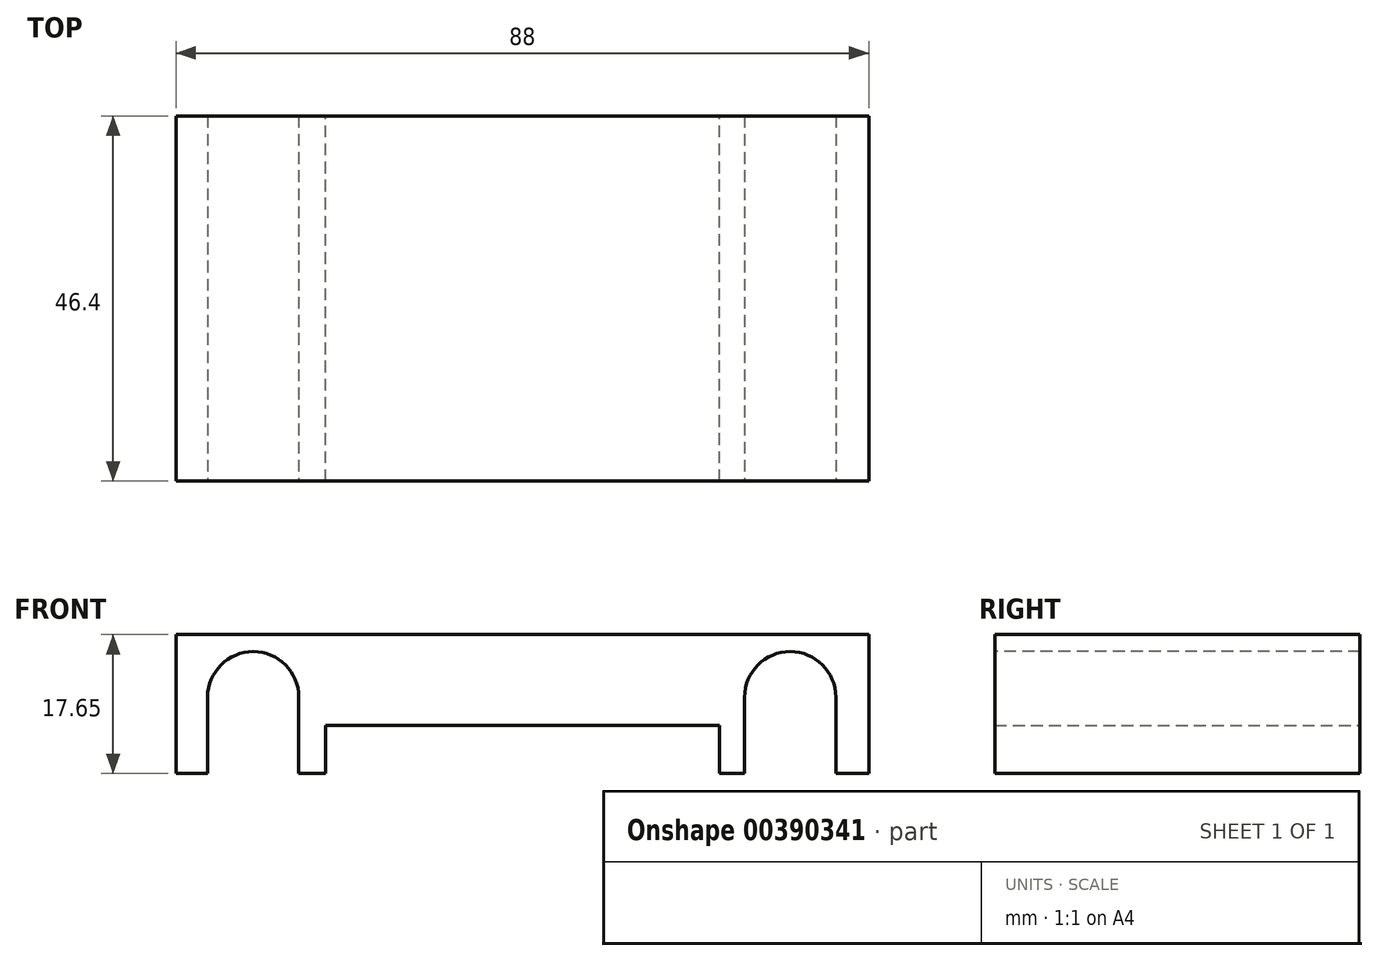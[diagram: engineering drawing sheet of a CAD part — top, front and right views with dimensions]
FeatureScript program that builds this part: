
annotation { "Feature Type Name" : "Feature", "Feature Type Description" : "" }
export const myFeature = defineFeature(function(context is Context, id is Id, definition is map)
    precondition{}
    {
        {
            var Q0;
            Q0=qCreatedBy(makeId("Top.planeOp"),FACE);
            var sketch = newSketch(context, id + "F0", { "sketchPlane" : qUnion([Q0])});
            skLineSegment(sketch, "E0.bottom", {"start": v(44, 23.2) * mm, "end": v(-44, 23.2) * mm});
            skLineSegment(sketch, "E0.top", {"start": v(44, -23.2) * mm, "end": v(-44, -23.2) * mm});
            skLineSegment(sketch, "E0.left", {"start": v(44, 23.2) * mm, "end": v(44, -23.2) * mm});
            skLineSegment(sketch, "E0.right", {"start": v(-44, 23.2) * mm, "end": v(-44, -23.2) * mm});
            skPoint(sketch, "E0.middle", {"position": v(0, 0) * mm});
            skSolve(sketch);
        }
        {
            var Q0;
            Q0 = qSketchRegion(id + "F0", true);
            extrude(context, id + "F1", {"entities" : qUnion([Q0]), "oppositeDirection" : true, "depth" : 17.65 * mm});
        }
        {
            var Q0;
            Q0=makeQuery(id+"F1.opExtrude","CAP_FACE",FACE,{"disambiguationData":[OSD([sQuery(id+"F0.wireOp",EDGE,"E0.bottom"),sQuery(id+"F0.wireOp",EDGE,"E0.top"),sQuery(id+"F0.wireOp",EDGE,"E0.left"),sQuery(id+"F0.wireOp",EDGE,"E0.right")])],"isStart":false});
            var sketch = newSketch(context, id + "F2", { "sketchPlane" : qUnion([Q0])});
            skLineSegment(sketch, "E1.bottom", {"start": v(-25, 23.2) * mm, "end": v(25, 23.2) * mm});
            skLineSegment(sketch, "E1.top", {"start": v(-25, -23.2) * mm, "end": v(25, -23.2) * mm});
            skLineSegment(sketch, "E1.left", {"start": v(-25, 23.2) * mm, "end": v(-25, -23.2) * mm});
            skLineSegment(sketch, "E1.right", {"start": v(25, 23.2) * mm, "end": v(25, -23.2) * mm});
            skSolve(sketch);
        }
        {
            var Q0;
            Q0 = qSketchRegion(id + "F2", true);
            extrude(context, id + "F3", {"entities" : qUnion([Q0]), "operationType" : NewBodyOperationType.REMOVE, "oppositeDirection" : true, "depth" : 6.15 * mm});
        }
        {
            var Q0;
            Q0=qCreatedBy(makeId("Front.planeOp"),FACE);
            var sketch = newSketch(context, id + "F4", { "sketchPlane" : qUnion([Q0])});
            skLineSegment(sketch, "E2.0.0", {"start": v(-25, -11.5) * mm, "end": v(25, -11.5) * mm, "construction": true});
            skLineSegment(sketch, "E2.0.1", {"start": v(25, -11.5) * mm, "end": v(25, -17.65) * mm, "construction": true});
            skLineSegment(sketch, "E2.0.2", {"start": v(25, -17.65) * mm, "end": v(44, -17.65) * mm, "construction": true});
            skLineSegment(sketch, "E2.0.3", {"start": v(44, -17.65) * mm, "end": v(44, 0) * mm, "construction": true});
            skLineSegment(sketch, "E2.0.4", {"start": v(44, 0) * mm, "end": v(-44, 0) * mm, "construction": true});
            skLineSegment(sketch, "E2.0.5", {"start": v(-44, 0) * mm, "end": v(-44, -17.65) * mm, "construction": true});
            skLineSegment(sketch, "E2.0.6", {"start": v(-44, -17.65) * mm, "end": v(-25, -17.65) * mm, "construction": true});
            skLineSegment(sketch, "E2.0.7", {"start": v(-25, -17.65) * mm, "end": v(-25, -11.5) * mm, "construction": true});
            skLineSegment(sketch, "E3.bottom", {"start": v(-40, -17.65) * mm, "end": v(-28.4, -17.65) * mm});
            skLineSegment(sketch, "E3.top", {"start": v(-40, -7.95) * mm, "end": v(-28.4, -7.95) * mm, "construction": true});
            skLineSegment(sketch, "E3.left", {"start": v(-40, -17.65) * mm, "end": v(-40, -7.95) * mm});
            skLineSegment(sketch, "E3.right", {"start": v(-28.4, -17.65) * mm, "end": v(-28.4, -7.95) * mm});
            skArc(sketch, "E4", {"start": v(-28.4, -7.95) * mm, "mid": v(-34.2, -2.15) * mm, "end": v(-40, -7.95) * mm});
            skLineSegment(sketch, "E5.bottom", {"start": v(28.2, -17.65) * mm, "end": v(39.8, -17.65) * mm});
            skLineSegment(sketch, "E5.top", {"start": v(28.2, -7.95) * mm, "end": v(39.8, -7.95) * mm, "construction": true});
            skLineSegment(sketch, "E5.left", {"start": v(28.2, -17.65) * mm, "end": v(28.2, -7.95) * mm});
            skLineSegment(sketch, "E5.right", {"start": v(39.8, -17.65) * mm, "end": v(39.8, -7.95) * mm});
            skArc(sketch, "E6", {"start": v(39.8, -7.95) * mm, "mid": v(34, -2.15) * mm, "end": v(28.2, -7.95) * mm});
            skSolve(sketch);
        }
        {
            var Q0;
            Q0 = qSketchRegion(id + "F4", true);
            extrude(context, id + "F5", {"entities" : qUnion([Q0]), "operationType" : NewBodyOperationType.REMOVE, "endBound" : BoundingType.THROUGH_ALL, "oppositeDirection" : true, "depth" : 25 * mm, "hasSecondDirection" : true, "secondDirectionBound" : SecondDirectionBoundingType.THROUGH_ALL, "secondDirectionOppositeDirection" : false, "secondDirectionDepth" : 25 * mm});
        }
    });
